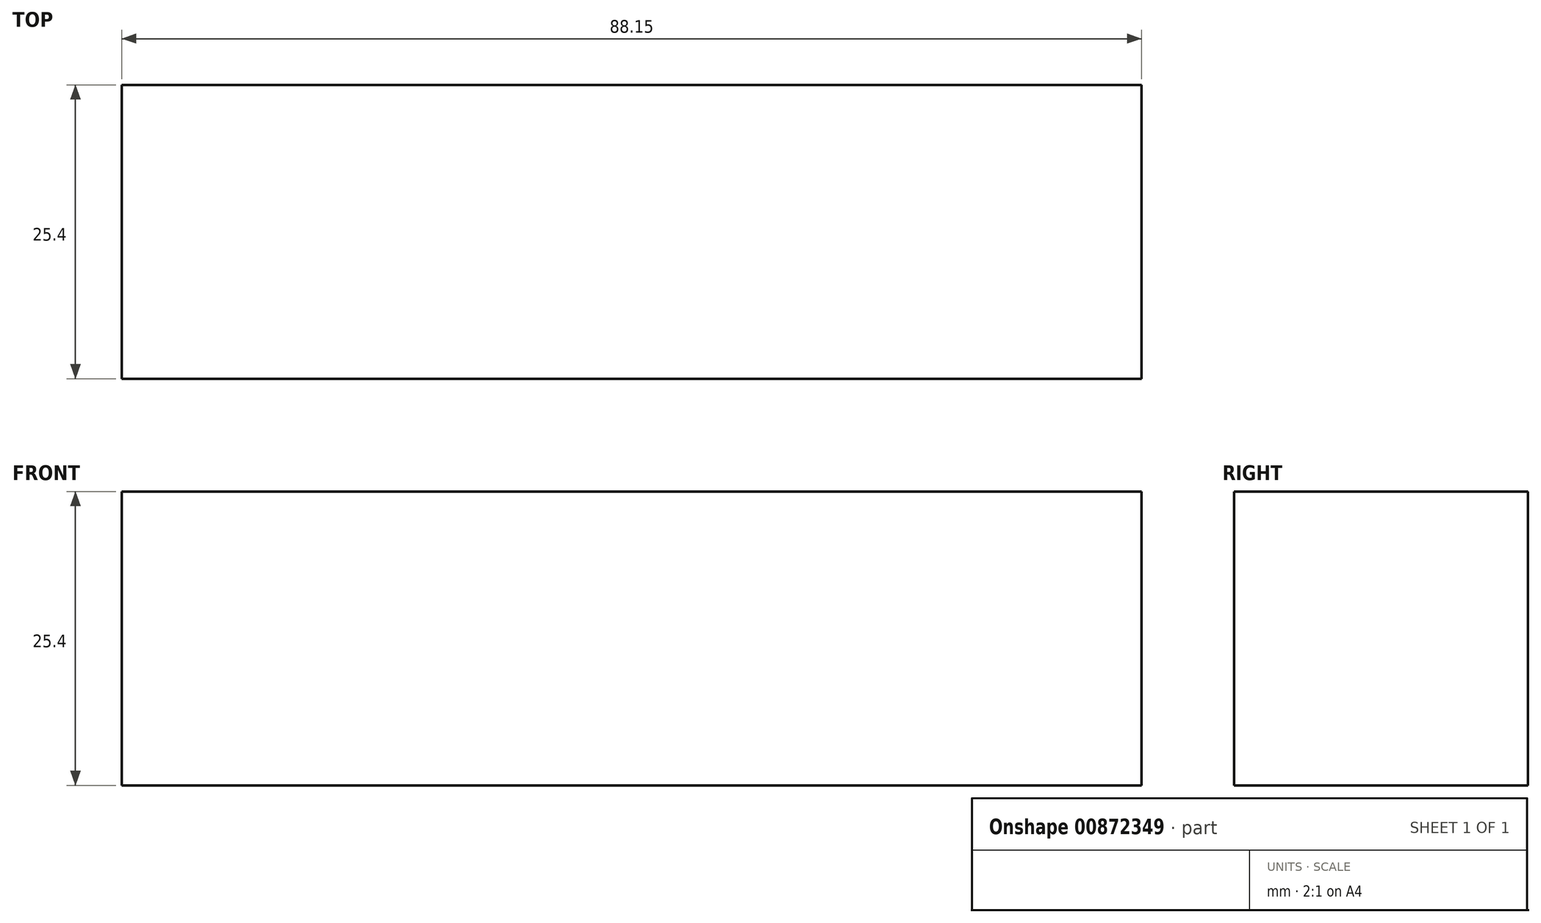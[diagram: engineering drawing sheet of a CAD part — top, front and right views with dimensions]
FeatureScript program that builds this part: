
annotation { "Feature Type Name" : "Feature", "Feature Type Description" : "" }
export const myFeature = defineFeature(function(context is Context, id is Id, definition is map)
    precondition{}
    {
        {
            var Q0;
            Q0=qCreatedBy(makeId("Front.planeOp"),FACE);
            var sketch = newSketch(context, id + "F0", { "sketchPlane" : qUnion([Q0])});
            skLineSegment(sketch, "E0", {"start": v(0, 0) * mm, "end": v(137.38, 0) * mm});
            skLineSegment(sketch, "E1", {"start": v(137.38, 0) * mm, "end": v(0, 0) * mm});
            skLineSegment(sketch, "E2", {"start": v(0, 0) * mm, "end": v(0, -25.4) * mm});
            skLineSegment(sketch, "E3", {"start": v(0, -25.4) * mm, "end": v(137.38, -25.4) * mm});
            skArc(sketch, "E4", {"start": v(137.38, 0) * mm, "mid": v(150.08, -12.7) * mm, "end": v(137.38, -25.4) * mm});
            skLineSegment(sketch, "E5.bottom", {"start": v(46.54, 0) * mm, "end": v(88.15, 0) * mm});
            skLineSegment(sketch, "E5.top", {"start": v(46.54, -25.4) * mm, "end": v(88.15, -25.4) * mm});
            skLineSegment(sketch, "E5.left", {"start": v(46.54, 0) * mm, "end": v(46.54, -25.4) * mm});
            skLineSegment(sketch, "E5.right", {"start": v(88.15, 0) * mm, "end": v(88.15, -25.4) * mm});
            skSolve(sketch);
        }
        {
            var Q0;
            {var subQ3=sQuery(id+"F0.wireOp",EDGE,"E5.left");var subQ8=makeQuery(id+"F0.imprint","IMPRINT",EDGE,{"derivedFrom":subQ3});var subQ10=sQuery(id+"F0.wireOp",EDGE,"E2");var subQ11=sQuery(id+"F0.wireOp",EDGE,"E4");Q0=qUnion([makeQuery(id+"F0.imprint","IMPRINT",FACE,{"disambiguationData":[TD([[makeQuery(id+"F0.imprint","IMPRINT",EDGE,{"derivedFrom":subQ11}),-1.0]])]}),makeQuery(id+"F0.imprint","IMPRINT",FACE,{"disambiguationData":[TD([[makeQuery(id+"F0.imprint","IMPRINT",EDGE,{"derivedFrom":subQ10}),1.0]])]}),makeQuery(id+"F0.imprint","IMPRINT",FACE,{"disambiguationData":[TD([[subQ8,1.0]])]})]);}
            extrude(context, id + "F1", {"entities" : qUnion([Q0]), "depth" : 25.4 * mm, "offsetDistance" : 25.4 * mm});
        }
    });
